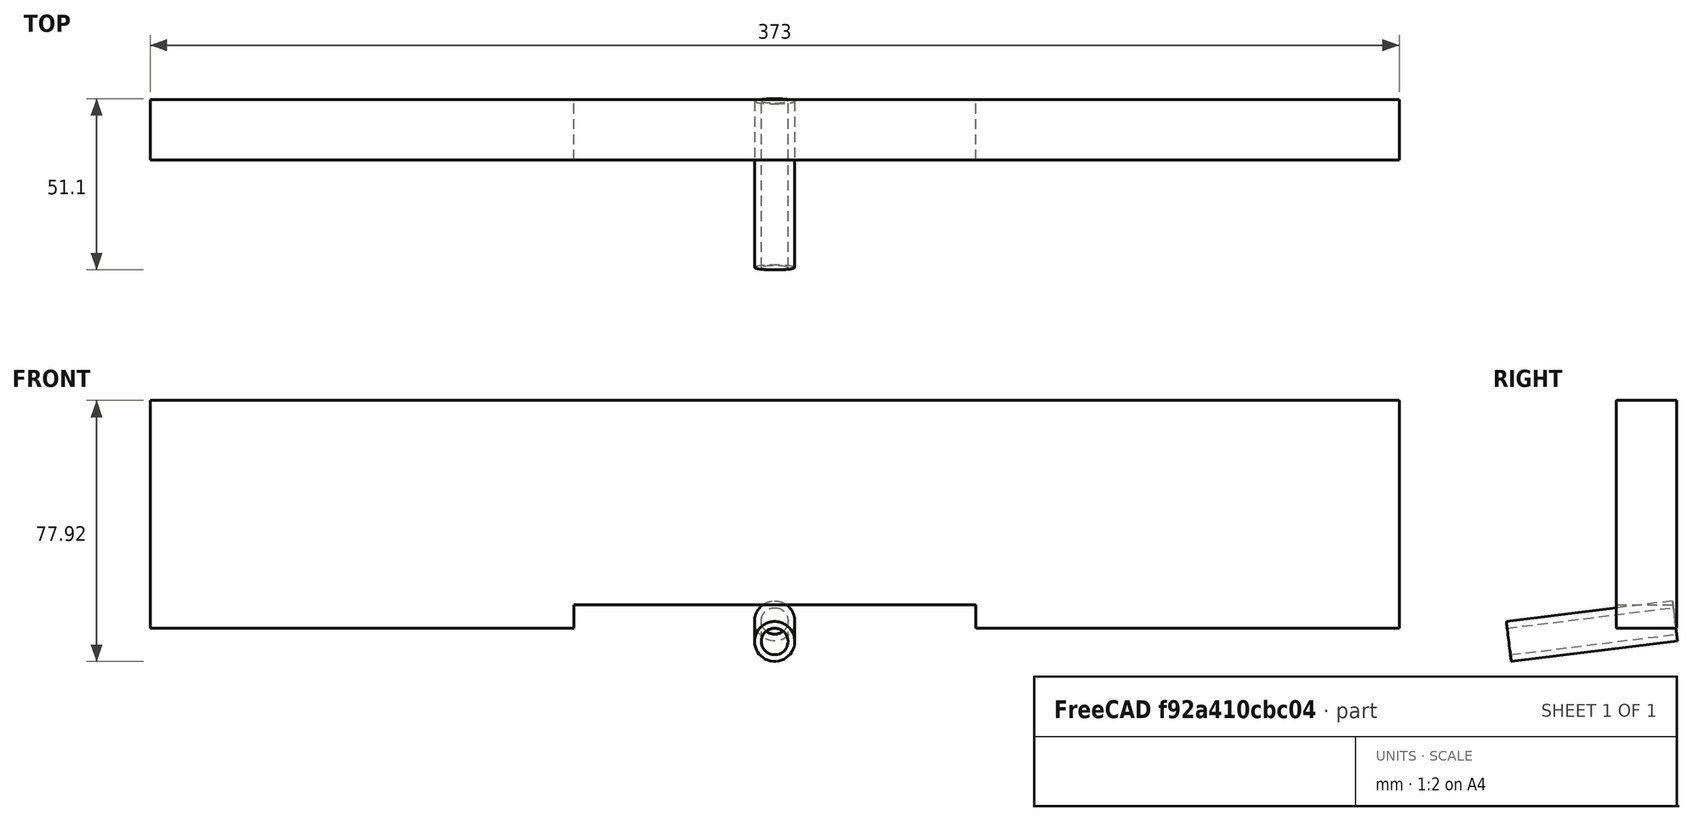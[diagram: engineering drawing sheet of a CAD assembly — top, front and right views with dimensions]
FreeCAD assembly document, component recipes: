
FREECAD ASSEMBLY — COMPONENT RECIPES ("podnica_pokrovcek")

This assembly document has 3 components, labeled P0..P2 below (a component is one placed body or linked part). 2 of them carry a construction recipe — the FreeCAD feature program that regenerates the part from scratch, quoted from this document or its linked companion documents; the rest are supplied as boundary geometry only. No exploded tour is included for this assembly.
COMPONENT P0 — geometry summary ("pokrovcek_smukalnik"; no construction recipe available for this part):
  bounding box: 373.0 x 68.0 x 18.0 mm
  tessellated surface: 268 triangles
  volume: 420905 mm^3 (92% of its bounding box)
  symmetry: 2-fold rotationally symmetric about the z axis; mirror-symmetric across its x mid-plane, y mid-plane
COMPONENT P1 — recipe-attached ("cevka", modeled in this document).
Construction recipe (the document's own serialized feature program — sketch geometry with constraints, then the solid features built on it; lengths are millimeters unless a unit is written):

FEATURE [PartDesign::CoordinateSystem] LCS_0003
  AttacherType = Attacher::AttachEngine3D
  MapMode = 2
  Support = -> [X_Axis006]
FEATURE [Sketcher::SketchObject] Sketch006
  FullyConstrained = true
  MapMode = 5
  Placement = pos=(0,0,0) rot=(0.57735,0.57735,0.57735;2.0944rad)
  Support = -> [YZ_Plane006]
  sketch-geometry (5):
    g0: LineSegment StartX=-32.6227 StartY=0 StartZ=0 EndX=17 EndY=6.1307 EndZ=0
    g1: LineSegment StartX=17 StartY=6.1307 StartZ=0 EndX=16.7548 EndY=8.11561 EndZ=0
    g2: LineSegment StartX=16.7548 StartY=8.11561 StartZ=0 EndX=-32.868 EndY=1.98491 EndZ=0
    g3: LineSegment StartX=-32.868 StartY=1.98491 StartZ=0 EndX=-32.6227 EndY=0 EndZ=0
    g4: LineSegment StartX=-32.6227 StartY=-4.03041 StartZ=0 EndX=17 EndY=2.10028 EndZ=0
  constraints (16):
    c: Coincident(g0,g1)
    c: Coincident(g1,g2)
    c: Coincident(g2,g3)
    c: Coincident(g3,g0)
    c: Perpendicular(g1,g0)
    c: Perpendicular(g2,g1)
    c: Perpendicular(g3,g2)
    c: Distance(g-1,g0) = 4
    c: Distance(g-1,g2) = 6
    c: DistanceX(g-1,g0) = 17
    c: Distance(g2) = 50
    c: Horizontal(g0,g-1)
    c: PointOnObject(g-1,g4)
    c: Parallel(g4,g0)
    c: Vertical(g0,g4)
    c: Vertical(g0,g4)
FEATURE [PartDesign::Revolution] Revolution
  Angle = 360
  Axis = (1.52e-14,49.6227,6.1307)
  Base = (-1e-14,-32.6227,-4.03041)
  Placement = pos=(0,0,0) rot=(0.57735,0.57735,0.57735;2.0944rad)
  Profile = -> Sketch006
  ReferenceAxis = -> Sketch006 [Axis0]
FEATURE [Sketcher::SketchObject] Sketch007
  FullyConstrained = true
  MapMode = 5
  Placement = pos=(-9.1e-15,-32.1323,-3.96982) rot=(0.599592,0.599592,-0.530074;2.16676rad)
  Support = -> [Revolution]
FEATURE [PartDesign::Body] Body_3
  Group = -> [LCS_0003,Sketch006,Revolution,Sketch007]
  Origin = -> Origin006
  Tip = -> Revolution
COMPONENT P2 — recipe-attached ("pokrovcek_navaden", modeled in this document).
Construction recipe (the document's own serialized feature program — sketch geometry with constraints, then the solid features built on it; lengths are millimeters unless a unit is written):

FEATURE [PartDesign::CoordinateSystem] LCS_0001
  AttacherType = Attacher::AttachEngine3D
  MapMode = 2
  Support = -> [X_Axis004]
FEATURE [Sketcher::SketchObject] Sketch004
  FullyConstrained = true
  MapMode = 5
  Placement = pos=(0,0,0) rot=(1,0,0;1.5708rad)
  Support = -> [XZ_Plane004]
  expr: Constraints[18] = Sketch.Constraints.L
  expr: Constraints[19] = Sketch.Constraints.H
  expr: Constraints[20] = Sketch.Constraints.L2
  expr: Constraints[21] = Sketch.Constraints.H2
  sketch-geometry (8):
    g0: LineSegment StartX=-186.5 StartY=68 StartZ=0 EndX=186.5 EndY=68 EndZ=0
    g1: LineSegment StartX=186.5 StartY=68 StartZ=0 EndX=186.5 EndY=0 EndZ=0
    g2: LineSegment StartX=186.5 StartY=0 StartZ=0 EndX=60 EndY=0 EndZ=0
    g3: LineSegment StartX=60 StartY=0 StartZ=0 EndX=60 EndY=7 EndZ=0
    g4: LineSegment StartX=60 StartY=7 StartZ=0 EndX=-60 EndY=7 EndZ=0
    g5: LineSegment StartX=-60 StartY=7 StartZ=0 EndX=-60 EndY=0 EndZ=0
    g6: LineSegment StartX=-60 StartY=0 StartZ=0 EndX=-186.5 EndY=0 EndZ=0
    g7: LineSegment StartX=-186.5 StartY=0 StartZ=0 EndX=-186.5 EndY=68 EndZ=0
  constraints (23):
    c: Horizontal(g0)
    c: Coincident(g0,g1)
    c: Vertical(g1)
    c: Coincident(g1,g2)
    c: Horizontal(g2)
    c: Coincident(g2,g3)
    c: Vertical(g3)
    c: Coincident(g3,g4)
    c: Horizontal(g4)
    c: Coincident(g4,g5)
    c: Vertical(g5)
    c: Coincident(g5,g6)
    c: Horizontal(g6)
    c: Coincident(g6,g7)
    c: Coincident(g7,g0)
    c: Vertical(g7)
    c: Horizontal(g5,g2)
    c: Symmetric(g2,g5,g-1)
    c: DistanceX(g0,g0) = 373
    c: DistanceY(g7,g7) = 68
    c: DistanceX(g4,g4) = 120
    c: DistanceY(g5,g5) = 7
    c: Equal(g6,g2)
FEATURE [PartDesign::Pad] Pad001
  Direction = (1,1,1)
  Length = 18
  Length2 = 100
  Placement = pos=(0,0,0) rot=(1,0,0;1.5708rad)
  Profile = -> Sketch004
  Reversed = true
  Type = 0
  expr: Length = Pad.Length
FEATURE [Sketcher::SketchObject] Sketch005
  FullyConstrained = true
  MapMode = 5
  Placement = pos=(0,0,0) rot=(0.57735,0.57735,0.57735;2.0944rad)
  Support = -> [YZ_Plane004]
  sketch-geometry (4):
    g0: LineSegment StartX=-32.6227 StartY=0 StartZ=0 EndX=17 EndY=6.1307 EndZ=0
    g1: LineSegment StartX=17 StartY=6.1307 StartZ=0 EndX=16.7548 EndY=8.11561 EndZ=0
    g2: LineSegment StartX=16.7548 StartY=8.11561 StartZ=0 EndX=-32.868 EndY=1.98491 EndZ=0
    g3: LineSegment StartX=-32.868 StartY=1.98491 StartZ=0 EndX=-32.6227 EndY=0 EndZ=0
  constraints (12):
    c: Coincident(g0,g1)
    c: Coincident(g1,g2)
    c: Coincident(g2,g3)
    c: Coincident(g3,g0)
    c: Perpendicular(g1,g0)
    c: Perpendicular(g2,g1)
    c: Perpendicular(g3,g2)
    c: Distance(g-1,g0) = 4
    c: Distance(g-1,g2) = 6
    c: DistanceX(g-1,g0) = 17
    c: Distance(g2) = 50
    c: Horizontal(g0,g-1)
FEATURE [PartDesign::Body] Body_2
  Group = -> [LCS_0001,Sketch004,Pad001,Sketch005]
  Origin = -> Origin004
  Tip = -> Pad001
PROVENANCE & LICENSES
A FreeCAD (.FCStd) document from a public repository crawl; recipes are the document's own serialized feature recipes (and, for linked parts, companion documents' recipes).
License: apache-2.0.
